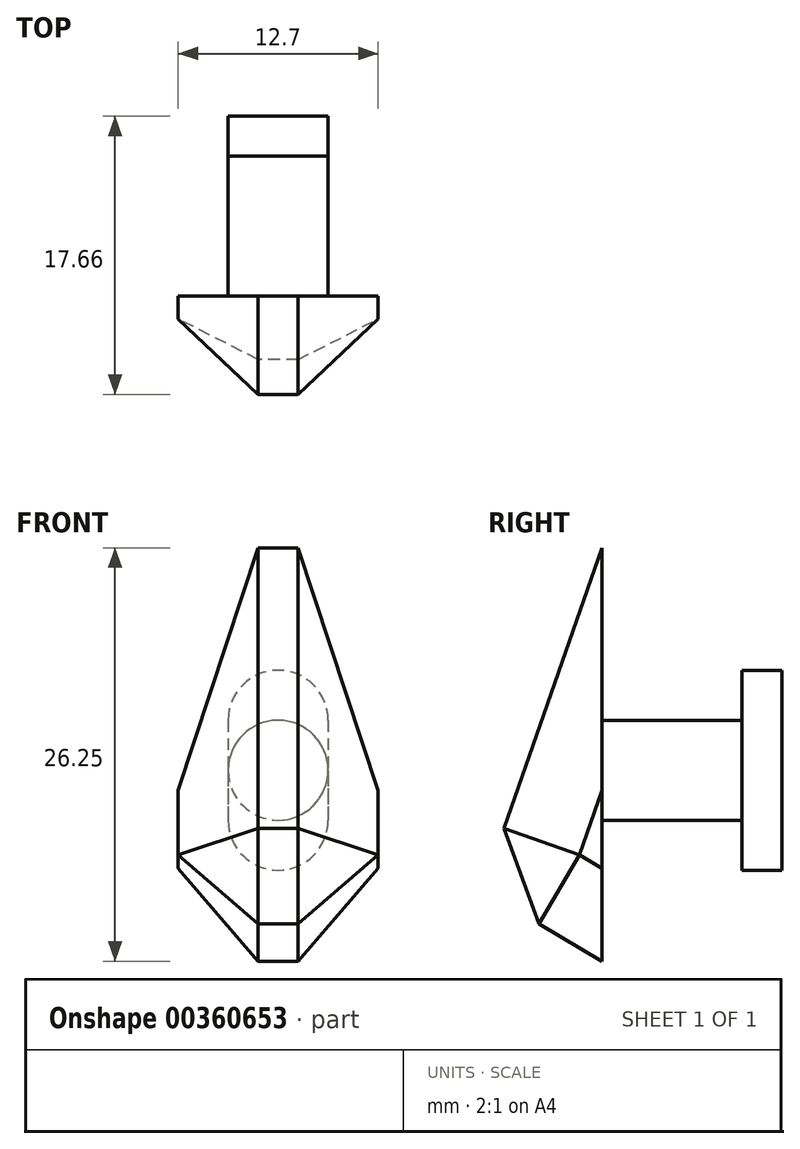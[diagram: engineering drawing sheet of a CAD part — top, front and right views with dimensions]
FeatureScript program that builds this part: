
annotation { "Feature Type Name" : "Feature", "Feature Type Description" : "" }
export const myFeature = defineFeature(function(context is Context, id is Id, definition is map)
    precondition{}
    {
        {
            var Q0;
            Q0=qCreatedBy(makeId("Front.planeOp"),FACE);
            var sketch = newSketch(context, id + "F0", { "sketchPlane" : qUnion([Q0])});
            skArc(sketch, "E0", {"start": v(-28.7, 40.47) * mm, "mid": v(-31.88, 43.65) * mm, "end": v(-35.05, 40.47) * mm});
            skArc(sketch, "E1", {"start": v(-35.05, 34.12) * mm, "mid": v(-31.88, 30.95) * mm, "end": v(-28.7, 34.12) * mm});
            skLineSegment(sketch, "E2", {"start": v(-35.05, 40.47) * mm, "end": v(-35.05, 34.12) * mm});
            skLineSegment(sketch, "E3", {"start": v(-28.7, 40.47) * mm, "end": v(-28.7, 34.12) * mm});
            skPoint(sketch, "E4", {"position": v(-31.88, 37.3) * mm});
            skPoint(sketch, "E5", {"position": v(-31.88, 43.65) * mm});
            skPoint(sketch, "E6", {"position": v(-31.88, 30.95) * mm});
            skSolve(sketch);
        }
        {
            var Q0;
            Q0 = qSketchRegion(id + "F0", true);
            extrude(context, id + "F1", {"entities" : qUnion([Q0]), "depth" : 2.54 * mm});
        }
        {
            var Q0;
            Q0=makeQuery(id+"F1.opExtrude","CAP_FACE",FACE,{"disambiguationData":[OSD([sQuery(id+"F0.wireOp",EDGE,"E0"),sQuery(id+"F0.wireOp",EDGE,"E1"),sQuery(id+"F0.wireOp",EDGE,"E2"),sQuery(id+"F0.wireOp",EDGE,"E3")])],"isStart":false});
            var sketch = newSketch(context, id + "F2", { "sketchPlane" : qUnion([Q0])});
            skLineSegment(sketch, "E7", {"start": v(-31.88, 43.65) * mm, "end": v(-31.88, 30.95) * mm, "construction": true});
            skLineSegment(sketch, "E8", {"start": v(-35.05, 37.3) * mm, "end": v(-31.88, 37.3) * mm, "construction": true});
            skCircle(sketch, "E9", {"center": v(-31.88, 37.3) * mm, "radius": 3.17 * mm});
            skSolve(sketch);
        }
        {
            var Q0;
            {var subQ0=sQuery(id+"F2.wireOp",EDGE,"E9");var subQ1=makeQuery(id+"F2.imprint","INTERSECT",VERTEX,{"derivedFrom":[makeQuery(id+"F1.opExtrude","CAP_EDGE",EDGE,{"disambiguationData":[OSD([sQuery(id+"F0.wireOp",EDGE,"E2")])],"isStart":false}),subQ0]});Q0=makeQuery(id+"F2.imprint","IMPRINT",FACE,{"disambiguationData":[TD([[makeQuery(id+"F2.imprint","IMPRINT",EDGE,{"disambiguationData":[TD([[subQ1,1.0]])],"derivedFrom":subQ0}),1.0]])]});}
            var Q1;
            Q1=sQuery(id+"F2.wireOp",EDGE,"E8");
            var Q2;
            Q2=sQuery(id+"F2.wireOp",EDGE,"E7");
            extrude(context, id + "F3", {"entities" : qUnion([Q0]), "operationType" : NewBodyOperationType.ADD, "surfaceEntities" : qUnion([Q1, Q2]), "depth" : 8.9 * mm});
        }
        {
            var Q0;
            Q0=makeQuery(id+"F1.opExtrude","SWEPT_FACE",FACE,{"disambiguationData":[OSD([sQuery(id+"F0.wireOp",EDGE,"E2")])]});
            var Q1;
            Q1=makeQuery(id+"F1.opExtrude","SWEPT_FACE",FACE,{"disambiguationData":[OSD([sQuery(id+"F0.wireOp",EDGE,"E3")])]});
            cPlane(context, id + "F4", {"entities" : qUnion([Q0, Q1]), "cplaneType" : CPlaneType.MID_PLANE, "offset" : 25.4 * mm, "width" : 152.4 * mm, "height" : 152.4 * mm});
        }
        {
            var Q0;
            Q0=qCreatedBy(id+"F4.planeOp",FACE);
            var sketch = newSketch(context, id + "F5", { "sketchPlane" : qUnion([Q0])});
            skLineSegment(sketch, "E10", {"start": v(11.43, 51.42) * mm, "end": v(11.43, 25.17) * mm});
            skLineSegment(sketch, "E11", {"start": v(11.43, 51.42) * mm, "end": v(19.03, 29.67) * mm});
            skLineSegment(sketch, "E12", {"start": v(19.03, 29.67) * mm, "end": v(11.43, 25.17) * mm});
            skSolve(sketch);
        }
        {
            var Q0;
            Q0 = qSketchRegion(id + "F5", true);
            extrude(context, id + "F6", {"entities" : qUnion([Q0]), "operationType" : NewBodyOperationType.ADD, "depth" : 6.35 * mm, "hasSecondDirection" : true, "secondDirectionOppositeDirection" : true, "secondDirectionDepth" : 6.35 * mm});
        }
        {
            var Q0;
            Q0=makeQuery(id+"F6.opExtrude","CAP_EDGE",EDGE,{"disambiguationData":[OSD([sQuery(id+"F5.wireOp",EDGE,"E11")])],"isStart":true});
            var Q1;
            Q1=makeQuery(id+"F6.opExtrude","CAP_EDGE",EDGE,{"disambiguationData":[OSD([sQuery(id+"F5.wireOp",EDGE,"E11")])],"isStart":false});
            var Q2;
            Q2=makeQuery(id+"F6.opExtrude","CAP_EDGE",EDGE,{"disambiguationData":[OSD([sQuery(id+"F5.wireOp",EDGE,"E12")])],"isStart":false});
            var Q3;
            Q3=makeQuery(id+"F6.opExtrude","CAP_EDGE",EDGE,{"disambiguationData":[OSD([sQuery(id+"F5.wireOp",EDGE,"E12")])],"isStart":true});
            var Q4;
            Q4=makeQuery(id+"F6.opExtrude","SWEPT_EDGE",EDGE,{"disambiguationData":[OSD([sQuery(id+"F5.wireOp",EDGE,"E11"),sQuery(id+"F5.wireOp",EDGE,"E12")])]});
            chamfer(context, id + "F7", {"entities" : qUnion([Q0, Q1, Q2, Q3, Q4]), "width" : 5.08 * mm, "tangentPropagation" : true});
        }
    });
